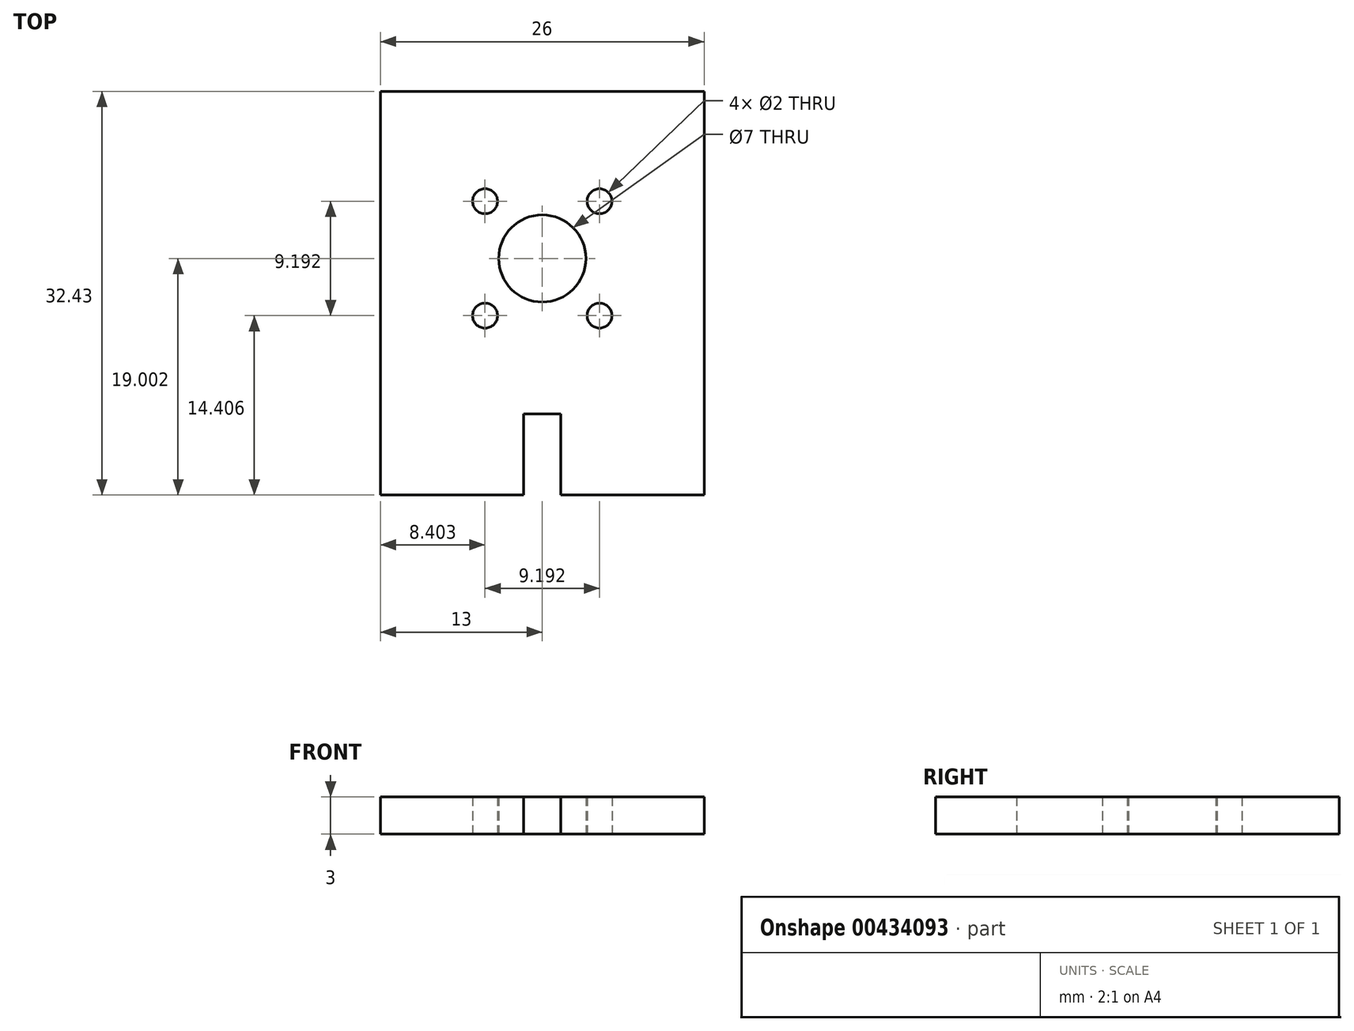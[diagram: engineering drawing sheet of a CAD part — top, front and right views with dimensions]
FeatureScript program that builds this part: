
annotation { "Feature Type Name" : "Feature", "Feature Type Description" : "" }
export const myFeature = defineFeature(function(context is Context, id is Id, definition is map)
    precondition{}
    {
        {
            var Q0;
            Q0=qCreatedBy(makeId("Top.planeOp"),FACE);
            var sketch = newSketch(context, id + "F0", { "sketchPlane" : qUnion([Q0])});
            skLineSegment(sketch, "E0", {"start": v(-216.4, -193.39) * mm, "end": v(-216.4, -327.3) * mm, "construction": true});
            skLineSegment(sketch, "E1", {"start": v(-237.43, -203.28) * mm, "end": v(-216.4, -203.28) * mm, "construction": true});
            skLineSegment(sketch, "E2", {"start": v(-216.4, -203.28) * mm, "end": v(-758.17, -203.28) * mm});
            skLineSegment(sketch, "E3", {"start": v(-768.17, -213.28) * mm, "end": v(-768.17, -312.5) * mm});
            skLineSegment(sketch, "E4", {"start": v(-216.4, -193.39) * mm, "end": v(-216.4, -56.57) * mm, "construction": true});
            skLineSegment(sketch, "E5", {"start": v(-216.4, -323.28) * mm, "end": v(-755.06, -323.28) * mm});
            skPoint(sketch, "E6.start.orphan", {"position": v(-216.4, -323.28) * mm});
            skLineSegment(sketch, "E7.0", {"start": v(-216.4, -213.28) * mm, "end": v(-768.17, -213.28) * mm});
            skLineSegment(sketch, "E8.0", {"start": v(-216.4, -318.28) * mm, "end": v(-765.68, -318.28) * mm});
            skLineSegment(sketch, "E9", {"start": v(-742.85, -318.28) * mm, "end": v(-742.85, -282.51) * mm});
            skLineSegment(sketch, "E10", {"start": v(-742.85, -282.51) * mm, "end": v(-742.85, -281.59) * mm});
            skLineSegment(sketch, "E11", {"start": v(-204.13, -279.09) * mm, "end": v(-768.17, -279.09) * mm, "construction": true});
            skLineSegment(sketch, "E12.0", {"start": v(-216.4, -276.59) * mm, "end": v(-747.57, -276.59) * mm});
            skLineSegment(sketch, "E13.0", {"start": v(-216.4, -281.59) * mm, "end": v(-747.57, -281.59) * mm});
            skLineSegment(sketch, "E14", {"start": v(-747.57, -281.59) * mm, "end": v(-747.57, -276.59) * mm});
            skLineSegment(sketch, "E15.trimOffspring", {"start": v(-742.85, -276.59) * mm, "end": v(-742.85, -213.28) * mm});
            skArc(sketch, "E16", {"start": v(-768.17, -213.28) * mm, "mid": v(-765.3, -206.28) * mm, "end": v(-758.37, -203.28) * mm});
            skFitSpline(sketch, "E17", {"points": [v(-768.17, -312.5) * mm, v(-767.64, -314.89) * mm, v(-766.5, -317.2) * mm, v(-764.5, -319.48) * mm, v(-762.87, -320.69) * mm, v(-761.52, -321.5) * mm, v(-759.85, -322.26) * mm, v(-758.32, -322.76) * mm, v(-758.3, -322.76) * mm, v(-758.3, -322.78) * mm, v(-755.06, -323.28) * mm], "startDerivative": vector(3.3, -19) * mm, "endDerivative": vector(33.17, -1.34) * mm});
            skLineSegment(sketch, "E18", {"start": v(26.78, 14.29) * mm, "end": v(55.78, 14.29) * mm, "construction": true});
            skLineSegment(sketch, "E19", {"start": v(171.63, -38.26) * mm, "end": v(138.63, -38.26) * mm, "construction": true});
            skLineSegment(sketch, "E20", {"start": v(-20.22, 54.29) * mm, "end": v(-20.22, 14.79) * mm, "construction": true});
            skLineSegment(sketch, "E21", {"start": v(59.78, 18.29) * mm, "end": v(59.78, 54.33) * mm, "construction": true});
            skLineSegment(sketch, "E22", {"start": v(-20.22, 54.29) * mm, "end": v(-16.22, 54.29) * mm, "construction": true});
            skLineSegment(sketch, "E23", {"start": v(-0.22, 58.29) * mm, "end": v(-0.22, 4.66) * mm, "construction": true});
            skPoint(sketch, "E23.endSnap0", {"position": v(-0.22, 54.29) * mm});
            skLineSegment(sketch, "E24", {"start": v(-16.22, 10.79) * mm, "end": v(15.78, 10.79) * mm, "construction": true});
            skPoint(sketch, "E25.startSnap0", {"position": v(20.78, 58.29) * mm});
            skLineSegment(sketch, "E26", {"start": v(19.78, 54.29) * mm, "end": v(19.78, 14.79) * mm, "construction": true});
            skPoint(sketch, "E27.0.start.orphan", {"position": v(19.78, 58.29) * mm});
            skLineSegment(sketch, "E28.0", {"start": v(-16.22, 57.79) * mm, "end": v(-16.22, 54.29) * mm});
            skLineSegment(sketch, "E29", {"start": v(-16.22, 57.79) * mm, "end": v(-16.22, 54.29) * mm, "construction": true});
            skPoint(sketch, "E30.orphan", {"position": v(-16.22, -36.82) * mm});
            skLineSegment(sketch, "E31.trimOffspring", {"start": v(-16.22, 10.79) * mm, "end": v(-16.22, 10.48) * mm, "construction": true});
            skLineSegment(sketch, "E32.trimOffspring", {"start": v(-16.22, 10.79) * mm, "end": v(-16.22, 10.48) * mm});
            skLineSegment(sketch, "E33.MirrorCS", {"start": v(15.78, 57.79) * mm, "end": v(15.78, 54.29) * mm, "construction": true});
            skLineSegment(sketch, "E34.0", {"start": v(-20.22, 14.79) * mm, "end": v(-16.22, 14.79) * mm});
            skLineSegment(sketch, "E35", {"start": v(-16.22, 14.79) * mm, "end": v(-16.22, 10.48) * mm, "construction": true});
            skLineSegment(sketch, "E36", {"start": v(15.78, 14.79) * mm, "end": v(15.78, 10.79) * mm, "construction": true});
            skLineSegment(sketch, "E37.trimOffspring", {"start": v(15.78, 14.79) * mm, "end": v(19.78, 14.79) * mm});
            skLineSegment(sketch, "E38.trimOffspring", {"start": v(15.78, 54.29) * mm, "end": v(19.78, 54.29) * mm, "construction": true});
            skLineSegment(sketch, "E39", {"start": v(-0.22, 51.23) * mm, "end": v(-8.97, 51.23) * mm});
            skLineSegment(sketch, "E40", {"start": v(-8.97, 51.23) * mm, "end": v(-12.82, 47.31) * mm});
            skLineSegment(sketch, "E41", {"start": v(-12.82, 47.31) * mm, "end": v(-12.82, 34.54) * mm});
            skLineSegment(sketch, "E42", {"start": v(19.78, 34.54) * mm, "end": v(-20.22, 34.54) * mm, "construction": true});
            skLineSegment(sketch, "E43.MirrorCS", {"start": v(-0.22, 51.23) * mm, "end": v(8.53, 51.23) * mm});
            skLineSegment(sketch, "E44.MirrorCS", {"start": v(8.53, 51.23) * mm, "end": v(12.38, 47.31) * mm});
            skLineSegment(sketch, "E45.MirrorCS", {"start": v(12.38, 47.31) * mm, "end": v(12.38, 34.54) * mm});
            skLineSegment(sketch, "E46.MirrorCS", {"start": v(-0.22, 17.85) * mm, "end": v(8.53, 17.85) * mm});
            skLineSegment(sketch, "E47.MirrorCS", {"start": v(-0.22, 17.85) * mm, "end": v(-8.97, 17.85) * mm});
            skLineSegment(sketch, "E48.MirrorCS", {"start": v(-8.97, 17.85) * mm, "end": v(-12.82, 21.76) * mm});
            skLineSegment(sketch, "E49.MirrorCS", {"start": v(-12.82, 21.76) * mm, "end": v(-12.82, 34.54) * mm});
            skLineSegment(sketch, "E50.MirrorCS", {"start": v(12.38, 21.76) * mm, "end": v(12.38, 34.54) * mm});
            skLineSegment(sketch, "E51.MirrorCS", {"start": v(8.53, 17.85) * mm, "end": v(12.38, 21.76) * mm});
            skLineSegment(sketch, "E52", {"start": v(-16.22, 57.79) * mm, "end": v(15.78, 57.79) * mm});
            skLineSegment(sketch, "E53", {"start": v(15.78, 54.29) * mm, "end": v(19.78, 54.29) * mm});
            skLineSegment(sketch, "E54", {"start": v(19.78, 14.79) * mm, "end": v(15.78, 14.79) * mm});
            skLineSegment(sketch, "E55", {"start": v(15.78, 10.79) * mm, "end": v(-16.22, 10.79) * mm});
            skLineSegment(sketch, "E56", {"start": v(-16.22, 14.79) * mm, "end": v(-20.22, 14.79) * mm});
            skLineSegment(sketch, "E57", {"start": v(-20.22, 54.29) * mm, "end": v(-20.22, 14.79) * mm});
            skLineSegment(sketch, "E58", {"start": v(-20.22, 54.29) * mm, "end": v(-16.22, 54.29) * mm});
            skLineSegment(sketch, "E59", {"start": v(19.78, 54.29) * mm, "end": v(19.78, 14.79) * mm});
            skLineSegment(sketch, "E60", {"start": v(15.78, 54.29) * mm, "end": v(15.78, 57.79) * mm});
            skLineSegment(sketch, "E61", {"start": v(15.78, 14.79) * mm, "end": v(15.78, 10.79) * mm});
            skLineSegment(sketch, "E62", {"start": v(-16.22, 14.79) * mm, "end": v(-16.22, 10.79) * mm});
            skLineSegment(sketch, "E63.0", {"start": v(55.78, 14.29) * mm, "end": v(55.78, 18.29) * mm});
            skLineSegment(sketch, "E64", {"start": v(22.78, 54.3) * mm, "end": v(26.78, 54.3) * mm, "construction": true});
            skLineSegment(sketch, "E65", {"start": v(22.78, 54.3) * mm, "end": v(22.78, 18.29) * mm, "construction": true});
            skLineSegment(sketch, "E66.0", {"start": v(26.78, 58.29) * mm, "end": v(26.78, 54.3) * mm});
            skLineSegment(sketch, "E67.0", {"start": v(22.78, 18.29) * mm, "end": v(26.78, 18.29) * mm});
            skPoint(sketch, "E68.orphan", {"position": v(25.41, 14.29) * mm});
            skLineSegment(sketch, "E69.trimOffspring", {"start": v(26.78, 18.29) * mm, "end": v(26.78, 14.29) * mm});
            skLineSegment(sketch, "E70.trimOffspring", {"start": v(55.78, 54.33) * mm, "end": v(55.78, 58.29) * mm});
            skLineSegment(sketch, "E71.trimOffspring", {"start": v(55.78, 18.29) * mm, "end": v(59.78, 18.29) * mm});
            skLineSegment(sketch, "E72", {"start": v(55.78, 14.29) * mm, "end": v(26.78, 14.29) * mm});
            skLineSegment(sketch, "E73", {"start": v(26.78, 18.29) * mm, "end": v(22.78, 18.29) * mm});
            skLineSegment(sketch, "E74", {"start": v(22.78, 18.29) * mm, "end": v(22.78, 54.3) * mm});
            skLineSegment(sketch, "E75", {"start": v(22.78, 54.3) * mm, "end": v(26.78, 54.3) * mm});
            skLineSegment(sketch, "E76", {"start": v(26.78, 58.29) * mm, "end": v(55.78, 58.29) * mm});
            skLineSegment(sketch, "E77", {"start": v(55.78, 54.33) * mm, "end": v(59.78, 54.33) * mm});
            skLineSegment(sketch, "E78", {"start": v(59.78, 54.33) * mm, "end": v(59.78, 18.75) * mm});
            skLineSegment(sketch, "E79.trimOffspring", {"start": v(55.78, 54.33) * mm, "end": v(59.78, 54.33) * mm, "construction": true});
            skPoint(sketch, "E80.orphan", {"position": v(61.78, 58.29) * mm});
            skLineSegment(sketch, "E81.trimOffspring", {"start": v(26.78, 58.29) * mm, "end": v(55.78, 58.29) * mm, "construction": true});
            skLineSegment(sketch, "E82", {"start": v(41.28, 58.29) * mm, "end": v(41.28, 14.29) * mm, "construction": true});
            skLineSegment(sketch, "E83", {"start": v(41.28, 51.1) * mm, "end": v(34.59, 51.1) * mm});
            skLineSegment(sketch, "E84", {"start": v(34.59, 51.1) * mm, "end": v(30.29, 47.53) * mm});
            skLineSegment(sketch, "E85", {"start": v(30.29, 47.53) * mm, "end": v(30.29, 36.34) * mm});
            skLineSegment(sketch, "E86.MirrorCS", {"start": v(41.28, 51.1) * mm, "end": v(47.97, 51.1) * mm});
            skLineSegment(sketch, "E87.MirrorCS", {"start": v(47.97, 51.1) * mm, "end": v(52.27, 47.53) * mm});
            skPoint(sketch, "E88.start.orphan", {"position": v(59.78, 38.29) * mm});
            skLineSegment(sketch, "E89", {"start": v(22.78, 36.29) * mm, "end": v(59.78, 36.54) * mm, "construction": true});
            skPoint(sketch, "E90.MirrorCS.end.orphan", {"position": v(52.27, 38.29) * mm});
            skPoint(sketch, "E90.MirrorCS.start.orphan", {"position": v(52.27, 47.53) * mm});
            skLineSegment(sketch, "E91", {"start": v(52.27, 47.53) * mm, "end": v(52.35, 36.5) * mm});
            skPoint(sketch, "E92.orphan", {"position": v(30.29, 38.29) * mm});
            skLineSegment(sketch, "E93.MirrorCS", {"start": v(41.48, 21.73) * mm, "end": v(48.18, 21.82) * mm});
            skLineSegment(sketch, "E94.MirrorCS", {"start": v(48.18, 21.82) * mm, "end": v(52.43, 25.45) * mm});
            skLineSegment(sketch, "E95.MirrorCS", {"start": v(52.43, 25.45) * mm, "end": v(52.35, 36.5) * mm});
            skLineSegment(sketch, "E96.MirrorCS", {"start": v(41.48, 21.73) * mm, "end": v(34.8, 21.63) * mm});
            skLineSegment(sketch, "E97.MirrorCS", {"start": v(34.8, 21.63) * mm, "end": v(30.44, 25.15) * mm});
            skLineSegment(sketch, "E98.MirrorCS", {"start": v(30.44, 25.15) * mm, "end": v(30.29, 36.34) * mm});
            skLineSegment(sketch, "E99", {"start": v(62.61, 49.29) * mm, "end": v(62.61, 18.29) * mm, "construction": true});
            skLineSegment(sketch, "E100", {"start": v(95.11, 49.29) * mm, "end": v(95.11, 18.29) * mm, "construction": true});
            skLineSegment(sketch, "E101", {"start": v(66.61, 53.29) * mm, "end": v(90.63, 53.29) * mm, "construction": true});
            skLineSegment(sketch, "E102.trimOffspring", {"start": v(62.61, 18.29) * mm, "end": v(66.61, 18.29) * mm});
            skLineSegment(sketch, "E103.0", {"start": v(91.11, 49.29) * mm, "end": v(95.11, 49.29) * mm});
            skLineSegment(sketch, "E104.0", {"start": v(66.61, 53.29) * mm, "end": v(66.61, 49.29) * mm});
            skLineSegment(sketch, "E105.0", {"start": v(91.11, 53.29) * mm, "end": v(91.11, 49.29) * mm});
            skLineSegment(sketch, "E106.trimOffspring", {"start": v(66.61, 14.29) * mm, "end": v(91.11, 14.29) * mm, "construction": true});
            skLineSegment(sketch, "E107.trimOffspring", {"start": v(91.11, 18.29) * mm, "end": v(95.11, 18.29) * mm});
            skLineSegment(sketch, "E108.trimOffspring", {"start": v(66.61, 18.29) * mm, "end": v(66.61, 14.29) * mm});
            skLineSegment(sketch, "E109.trimOffspring", {"start": v(91.11, 18.29) * mm, "end": v(91.11, 14.29) * mm});
            skLineSegment(sketch, "E110.trimOffspring", {"start": v(62.61, 49.29) * mm, "end": v(66.61, 49.29) * mm});
            skLineSegment(sketch, "E111", {"start": v(66.61, 53.29) * mm, "end": v(90.63, 53.29) * mm});
            skLineSegment(sketch, "E112", {"start": v(95.11, 49.29) * mm, "end": v(95.11, 18.29) * mm});
            skLineSegment(sketch, "E113", {"start": v(62.61, 49.29) * mm, "end": v(62.61, 18.29) * mm});
            skLineSegment(sketch, "E114", {"start": v(66.61, 14.29) * mm, "end": v(91.11, 14.29) * mm});
            skPoint(sketch, "E115.orphan", {"position": v(62.61, 49.98) * mm});
            skPoint(sketch, "E116.endSnap0", {"position": v(97.87, 14.29) * mm});
            skLineSegment(sketch, "E117", {"start": v(99.1, 41.57) * mm, "end": v(99.1, 18.29) * mm, "construction": true});
            skLineSegment(sketch, "E118.0", {"start": v(103.1, 14.29) * mm, "end": v(103.1, 18.29) * mm});
            skLineSegment(sketch, "E119.0", {"start": v(122.6, 14.29) * mm, "end": v(122.6, 18.29) * mm});
            skLineSegment(sketch, "E120.0", {"start": v(99.1, 41.79) * mm, "end": v(103.1, 41.79) * mm});
            skLineSegment(sketch, "E121.0", {"start": v(99.1, 18.29) * mm, "end": v(103.1, 18.29) * mm});
            skPoint(sketch, "E122.orphan", {"position": v(129.13, 14.29) * mm});
            skLineSegment(sketch, "E123.trimOffspring", {"start": v(126.6, 18.29) * mm, "end": v(126.6, 41.79) * mm});
            skLineSegment(sketch, "E124.trimOffspring", {"start": v(103.1, 45.79) * mm, "end": v(122.6, 45.79) * mm});
            skLineSegment(sketch, "E125.trimOffspring", {"start": v(103.1, 41.79) * mm, "end": v(103.1, 45.79) * mm});
            skLineSegment(sketch, "E126.trimOffspring", {"start": v(122.6, 41.79) * mm, "end": v(126.6, 41.79) * mm});
            skLineSegment(sketch, "E127.trimOffspring", {"start": v(122.6, 41.79) * mm, "end": v(122.6, 45.79) * mm});
            skLineSegment(sketch, "E128.trimOffspring", {"start": v(103.1, 14.29) * mm, "end": v(122.6, 14.29) * mm, "construction": true});
            skLineSegment(sketch, "E129.trimOffspring", {"start": v(99.1, 18.29) * mm, "end": v(99.1, 41.79) * mm, "construction": true});
            skLineSegment(sketch, "E130.trimOffspring", {"start": v(122.6, 18.29) * mm, "end": v(126.6, 18.29) * mm});
            skLineSegment(sketch, "E131", {"start": v(103.1, 14.29) * mm, "end": v(122.6, 14.29) * mm});
            skPoint(sketch, "E132.orphan", {"position": v(95.11, 14.29) * mm});
            skPoint(sketch, "E133.orphan", {"position": v(95.11, 49.68) * mm});
            skLineSegment(sketch, "E134", {"start": v(78.62, 53.29) * mm, "end": v(78.62, 14.29) * mm, "construction": true});
            skLineSegment(sketch, "E135", {"start": v(62.61, 33.79) * mm, "end": v(95.11, 33.79) * mm, "construction": true});
            skLineSegment(sketch, "E136", {"start": v(78.62, 47.64) * mm, "end": v(71.14, 47.64) * mm});
            skLineSegment(sketch, "E137", {"start": v(71.14, 47.64) * mm, "end": v(68.95, 45.1) * mm});
            skLineSegment(sketch, "E138", {"start": v(68.95, 45.1) * mm, "end": v(68.95, 33.79) * mm});
            skLineSegment(sketch, "E139.MirrorCS", {"start": v(78.62, 47.64) * mm, "end": v(86.1, 47.64) * mm});
            skLineSegment(sketch, "E140.MirrorCS", {"start": v(86.1, 47.64) * mm, "end": v(88.29, 45.1) * mm});
            skLineSegment(sketch, "E141.MirrorCS", {"start": v(88.29, 45.1) * mm, "end": v(88.29, 33.79) * mm});
            skLineSegment(sketch, "E142.MirrorCS", {"start": v(78.62, 19.94) * mm, "end": v(71.14, 19.94) * mm});
            skLineSegment(sketch, "E143.MirrorCS", {"start": v(71.14, 19.94) * mm, "end": v(68.95, 22.48) * mm});
            skLineSegment(sketch, "E144.MirrorCS", {"start": v(68.95, 22.48) * mm, "end": v(68.95, 33.79) * mm});
            skLineSegment(sketch, "E145.MirrorCS", {"start": v(78.62, 19.94) * mm, "end": v(86.1, 19.94) * mm});
            skLineSegment(sketch, "E146.MirrorCS", {"start": v(86.1, 19.94) * mm, "end": v(88.29, 22.48) * mm});
            skLineSegment(sketch, "E147.MirrorCS", {"start": v(88.29, 22.48) * mm, "end": v(88.29, 33.79) * mm});
            skLineSegment(sketch, "E148", {"start": v(112.85, 45.79) * mm, "end": v(112.85, 14.29) * mm, "construction": true});
            skLineSegment(sketch, "E149", {"start": v(99.1, 30.04) * mm, "end": v(126.6, 30.04) * mm, "construction": true});
            skLineSegment(sketch, "E150", {"start": v(112.85, 39.72) * mm, "end": v(107.14, 39.72) * mm});
            skLineSegment(sketch, "E151", {"start": v(107.14, 39.72) * mm, "end": v(105.12, 37.19) * mm});
            skLineSegment(sketch, "E152", {"start": v(105.12, 37.19) * mm, "end": v(105.12, 30.04) * mm});
            skLineSegment(sketch, "E153.MirrorCS", {"start": v(112.85, 39.72) * mm, "end": v(118.56, 39.72) * mm});
            skLineSegment(sketch, "E154.MirrorCS", {"start": v(118.56, 39.72) * mm, "end": v(120.59, 37.19) * mm});
            skLineSegment(sketch, "E155.MirrorCS", {"start": v(120.59, 37.19) * mm, "end": v(120.59, 30.04) * mm});
            skLineSegment(sketch, "E156.MirrorCS", {"start": v(118.56, 20.35) * mm, "end": v(120.59, 22.89) * mm});
            skLineSegment(sketch, "E157.MirrorCS", {"start": v(112.85, 20.35) * mm, "end": v(118.56, 20.35) * mm});
            skLineSegment(sketch, "E158.MirrorCS", {"start": v(112.85, 20.35) * mm, "end": v(107.14, 20.35) * mm});
            skLineSegment(sketch, "E159.MirrorCS", {"start": v(107.14, 20.35) * mm, "end": v(105.12, 22.89) * mm});
            skLineSegment(sketch, "E160.MirrorCS", {"start": v(105.12, 22.89) * mm, "end": v(105.12, 30.04) * mm});
            skLineSegment(sketch, "E161.MirrorCS", {"start": v(120.59, 22.89) * mm, "end": v(120.59, 30.04) * mm});
            skPoint(sketch, "E162.orphan", {"position": v(22.78, 14.29) * mm});
            skLineSegment(sketch, "E163", {"start": v(-7, 45.54) * mm, "end": v(6.03, 45.54) * mm, "construction": true});
            skLineSegment(sketch, "E164", {"start": v(-10.72, 27.54) * mm, "end": v(-10.72, 41.54) * mm, "construction": true});
            skPoint(sketch, "E164.endSnap0", {"position": v(-12.82, 40.93) * mm});
            skLineSegment(sketch, "E165.MirrorCS", {"start": v(10.28, 27.54) * mm, "end": v(10.28, 41.54) * mm, "construction": true});
            skLineSegment(sketch, "E166.MirrorCS", {"start": v(-7, 23.54) * mm, "end": v(6.03, 23.54) * mm, "construction": true});
            skLineSegment(sketch, "E167.0", {"start": v(-10.72, 41.54) * mm, "end": v(-6.72, 41.54) * mm});
            skLineSegment(sketch, "E168.0", {"start": v(-6.72, 23.54) * mm, "end": v(-6.72, 27.54) * mm});
            skPoint(sketch, "E169.orphan", {"position": v(-10.72, 40.93) * mm});
            skPoint(sketch, "E170.orphan", {"position": v(10.28, 40.93) * mm});
            skLineSegment(sketch, "E171.MirrorCS", {"start": v(-10.72, 27.54) * mm, "end": v(-6.72, 27.54) * mm});
            skLineSegment(sketch, "E172.MirrorCS", {"start": v(6.28, 23.54) * mm, "end": v(6.28, 27.54) * mm});
            skLineSegment(sketch, "E173", {"start": v(-6.72, 45.54) * mm, "end": v(6.03, 45.54) * mm});
            skLineSegment(sketch, "E174", {"start": v(-6.72, 23.54) * mm, "end": v(6.28, 23.54) * mm});
            skLineSegment(sketch, "E175", {"start": v(-10.72, 41.54) * mm, "end": v(-10.72, 27.54) * mm});
            skLineSegment(sketch, "E176.trimOffspring", {"start": v(6.28, 41.54) * mm, "end": v(10.28, 41.54) * mm});
            skLineSegment(sketch, "E177.trimOffspring", {"start": v(-6.72, 41.54) * mm, "end": v(-6.72, 45.54) * mm});
            skLineSegment(sketch, "E178.trimOffspring", {"start": v(6.28, 41.54) * mm, "end": v(6.28, 45.54) * mm});
            skLineSegment(sketch, "E179.trimOffspring", {"start": v(6.28, 27.54) * mm, "end": v(10.28, 27.54) * mm});
            skPoint(sketch, "E180.orphan", {"position": v(-10.72, 26.48) * mm});
            skPoint(sketch, "E181.orphan", {"position": v(10.28, 26.48) * mm});
            skLineSegment(sketch, "E182", {"start": v(10.28, 41.54) * mm, "end": v(10.28, 27.54) * mm});
            skPoint(sketch, "E183.orphan", {"position": v(-20.22, 10.79) * mm});
            skLineSegment(sketch, "E184.trimOffspring", {"start": v(-20.22, -9.83) * mm, "end": v(-20.22, -34.26) * mm, "construction": true});
            skPoint(sketch, "E185.orphan", {"position": v(19.78, 10.79) * mm});
            skLineSegment(sketch, "E186", {"start": v(5.78, -9.83) * mm, "end": v(5.78, -34.26) * mm, "construction": true});
            skLineSegment(sketch, "E187", {"start": v(8.94, -34.33) * mm, "end": v(8.94, 1.17) * mm, "construction": true});
            skLineSegment(sketch, "E188.trimOffspring", {"start": v(1.78, -38.26) * mm, "end": v(-5.72, -38.26) * mm, "construction": true});
            skLineSegment(sketch, "E189", {"start": v(12.94, 5.17) * mm, "end": v(40.94, 5.17) * mm, "construction": true});
            skLineSegment(sketch, "E190", {"start": v(44.94, 1.17) * mm, "end": v(44.94, -34.33) * mm, "construction": true});
            skLineSegment(sketch, "E191", {"start": v(87.34, -34.33) * mm, "end": v(87.34, 6.67) * mm, "construction": true});
            skPoint(sketch, "E192.orphan", {"position": v(88.24, 10.67) * mm});
            skLineSegment(sketch, "E193", {"start": v(94.23, 11.74) * mm, "end": v(127.23, 11.74) * mm, "construction": true});
            skLineSegment(sketch, "E194", {"start": v(131.23, 7.74) * mm, "end": v(131.23, -34.26) * mm, "construction": true});
            skLineSegment(sketch, "E195", {"start": v(90.23, 7.74) * mm, "end": v(90.23, -34.26) * mm, "construction": true});
            skLineSegment(sketch, "E196", {"start": v(134.63, 7.74) * mm, "end": v(134.63, 5.1) * mm, "construction": true});
            skPoint(sketch, "E196.startSnap0", {"position": v(134.63, 11.74) * mm});
            skLineSegment(sketch, "E197", {"start": v(175.63, 7.74) * mm, "end": v(175.63, -34.26) * mm, "construction": true});
            skPoint(sketch, "E198.orphan", {"position": v(93.98, 11.74) * mm});
            skLineSegment(sketch, "E199", {"start": v(134.63, 7.74) * mm, "end": v(134.63, -34.26) * mm, "construction": true});
            skLineSegment(sketch, "E200.trimOffspring", {"start": v(138.63, 11.74) * mm, "end": v(171.63, 11.74) * mm, "construction": true});
            skLineSegment(sketch, "E201.trimOffspring", {"start": v(127.23, -38.26) * mm, "end": v(112.23, -38.26) * mm, "construction": true});
            skLineSegment(sketch, "E202", {"start": v(-7.22, -5.83) * mm, "end": v(-7.22, -38.26) * mm, "construction": true});
            skLineSegment(sketch, "E203", {"start": v(26.94, 5.17) * mm, "end": v(26.94, -38.33) * mm, "construction": true});
            skLineSegment(sketch, "E204", {"start": v(67.17, 10.67) * mm, "end": v(67.34, -38.33) * mm, "construction": true});
            skLineSegment(sketch, "E205", {"start": v(110.73, 11.74) * mm, "end": v(110.73, -38.26) * mm, "construction": true});
            skLineSegment(sketch, "E206", {"start": v(154.96, 11.74) * mm, "end": v(155.13, -38.26) * mm, "construction": true});
            skLineSegment(sketch, "E207.0", {"start": v(109.23, -25.26) * mm, "end": v(109.23, -38.26) * mm, "construction": true});
            skLineSegment(sketch, "E208.0", {"start": v(112.23, -25.26) * mm, "end": v(112.23, -38.26) * mm});
            skLineSegment(sketch, "E209.0", {"start": v(112.23, -25.26) * mm, "end": v(109.23, -25.26) * mm, "construction": true});
            skLineSegment(sketch, "E210", {"start": v(109.23, -38.26) * mm, "end": v(109.23, -25.26) * mm});
            skLineSegment(sketch, "E211", {"start": v(112.23, -25.26) * mm, "end": v(109.23, -25.26) * mm});
            skLineSegment(sketch, "E212.trimOffspring", {"start": v(109.23, -38.26) * mm, "end": v(94.23, -38.26) * mm, "construction": true});
            skLineSegment(sketch, "E213.0", {"start": v(175.63, -34.26) * mm, "end": v(171.63, -34.26) * mm});
            skLineSegment(sketch, "E214.0", {"start": v(171.63, 11.74) * mm, "end": v(171.63, 7.74) * mm, "construction": true});
            skLineSegment(sketch, "E215.0", {"start": v(134.63, 7.74) * mm, "end": v(138.63, 7.74) * mm, "construction": true});
            skLineSegment(sketch, "E216.0", {"start": v(138.63, 11.74) * mm, "end": v(138.63, 7.74) * mm, "construction": true});
            skLineSegment(sketch, "E217.trimOffspring", {"start": v(171.63, 7.74) * mm, "end": v(175.63, 7.74) * mm, "construction": true});
            skLineSegment(sketch, "E218.trimOffspring", {"start": v(138.63, -34.26) * mm, "end": v(134.63, -34.26) * mm});
            skLineSegment(sketch, "E219.trimOffspring", {"start": v(138.63, -34.26) * mm, "end": v(138.63, -38.26) * mm, "construction": true});
            skLineSegment(sketch, "E220.trimOffspring", {"start": v(171.63, -34.26) * mm, "end": v(171.63, -38.26) * mm, "construction": true});
            skPoint(sketch, "E221.orphan", {"position": v(175.28, 11.74) * mm});
            skPoint(sketch, "E222.orphan", {"position": v(175.63, 11.74) * mm});
            skPoint(sketch, "E223.orphan", {"position": v(134.63, -38.26) * mm});
            skPoint(sketch, "E224.orphan", {"position": v(175.63, -38.26) * mm});
            skLineSegment(sketch, "E225.0", {"start": v(127.23, 11.74) * mm, "end": v(127.23, 7.74) * mm});
            skLineSegment(sketch, "E226.0", {"start": v(94.23, 11.74) * mm, "end": v(94.23, 7.74) * mm});
            skLineSegment(sketch, "E227.0", {"start": v(90.23, 7.74) * mm, "end": v(94.23, 7.74) * mm, "construction": true});
            skLineSegment(sketch, "E228.0", {"start": v(94.23, -34.26) * mm, "end": v(90.23, -34.26) * mm, "construction": true});
            skLineSegment(sketch, "E229.0", {"start": v(131.23, -34.26) * mm, "end": v(127.23, -34.26) * mm, "construction": true});
            skLineSegment(sketch, "E230.trimOffspring", {"start": v(127.23, 7.74) * mm, "end": v(131.23, 7.74) * mm, "construction": true});
            skLineSegment(sketch, "E231.trimOffspring", {"start": v(94.23, -34.26) * mm, "end": v(94.23, -38.26) * mm});
            skPoint(sketch, "E232.orphan", {"position": v(90.23, -38.26) * mm});
            skPoint(sketch, "E233.orphan", {"position": v(90.23, 11.74) * mm});
            skPoint(sketch, "E234.orphan", {"position": v(131.23, 11.74) * mm});
            skLineSegment(sketch, "E235", {"start": v(94.23, -38.26) * mm, "end": v(109.23, -38.26) * mm});
            skLineSegment(sketch, "E236", {"start": v(90.23, 7.74) * mm, "end": v(90.23, -34.26) * mm});
            skLineSegment(sketch, "E237", {"start": v(90.23, -34.26) * mm, "end": v(94.23, -34.26) * mm});
            skLineSegment(sketch, "E238", {"start": v(127.23, -34.26) * mm, "end": v(131.23, -34.26) * mm});
            skLineSegment(sketch, "E239", {"start": v(131.23, -34.26) * mm, "end": v(131.23, 7.74) * mm});
            skLineSegment(sketch, "E240", {"start": v(131.23, 7.74) * mm, "end": v(127.23, 7.74) * mm});
            skLineSegment(sketch, "E241", {"start": v(94.23, 11.74) * mm, "end": v(127.23, 11.74) * mm});
            skPoint(sketch, "E242.orphan", {"position": v(131.23, -38.26) * mm});
            skLineSegment(sketch, "E243.trimOffspring", {"start": v(127.23, -34.26) * mm, "end": v(127.23, -38.26) * mm});
            skLineSegment(sketch, "E244.trimOffspring", {"start": v(112.23, -38.26) * mm, "end": v(127.23, -38.26) * mm});
            skLineSegment(sketch, "E245", {"start": v(138.63, 11.74) * mm, "end": v(171.63, 11.74) * mm});
            skLineSegment(sketch, "E246", {"start": v(171.63, 7.74) * mm, "end": v(175.63, 7.74) * mm});
            skLineSegment(sketch, "E247", {"start": v(175.63, 7.74) * mm, "end": v(175.63, -34.26) * mm});
            skLineSegment(sketch, "E248", {"start": v(138.63, -38.26) * mm, "end": v(171.63, -38.26) * mm});
            skLineSegment(sketch, "E249", {"start": v(171.63, -38.26) * mm, "end": v(171.63, -34.26) * mm});
            skLineSegment(sketch, "E250", {"start": v(138.63, -38.26) * mm, "end": v(138.63, -34.26) * mm});
            skLineSegment(sketch, "E251", {"start": v(134.63, -34.26) * mm, "end": v(134.63, 7.74) * mm});
            skLineSegment(sketch, "E252", {"start": v(138.63, 7.74) * mm, "end": v(138.63, 11.74) * mm});
            skLineSegment(sketch, "E253", {"start": v(94.23, 7.74) * mm, "end": v(90.23, 7.74) * mm});
            skLineSegment(sketch, "E254", {"start": v(138.63, 7.74) * mm, "end": v(134.63, 7.74) * mm});
            skLineSegment(sketch, "E255", {"start": v(171.63, 7.74) * mm, "end": v(171.63, 11.74) * mm});
            skLineSegment(sketch, "E256", {"start": v(54.82, -17.76) * mm, "end": v(79.71, -17.68) * mm, "construction": true});
            skLineSegment(sketch, "E257", {"start": v(141.1, -17.47) * mm, "end": v(141.04, 1.05) * mm});
            skLineSegment(sketch, "E258", {"start": v(141.04, 1.05) * mm, "end": v(144.02, 4.5) * mm});
            skLineSegment(sketch, "E259", {"start": v(144.02, 4.5) * mm, "end": v(154.98, 4.5) * mm});
            skLineSegment(sketch, "E260", {"start": v(141.1, -17.47) * mm, "end": v(155.06, -17.47) * mm});
            skLineSegment(sketch, "E261.trimOffspring", {"start": v(141.1, -17.47) * mm, "end": v(167.9, -17.38) * mm, "construction": true});
            skLineSegment(sketch, "E262.trimOffspring", {"start": v(97.04, -17.62) * mm, "end": v(110.73, -17.57) * mm, "construction": true});
            skLineSegment(sketch, "E263.MirrorCS", {"start": v(169, -17.37) * mm, "end": v(155.06, -17.47) * mm});
            skLineSegment(sketch, "E264.MirrorCS", {"start": v(169, -17.37) * mm, "end": v(168.94, 1.14) * mm});
            skLineSegment(sketch, "E265.MirrorCS", {"start": v(168.94, 1.14) * mm, "end": v(165.94, 4.57) * mm});
            skLineSegment(sketch, "E266", {"start": v(110.73, -17.57) * mm, "end": v(97.04, -17.62) * mm});
            skLineSegment(sketch, "E267", {"start": v(97.04, 1.2) * mm, "end": v(99.73, 4.04) * mm});
            skLineSegment(sketch, "E268", {"start": v(99.73, 4.04) * mm, "end": v(110.73, 4.04) * mm});
            skPoint(sketch, "E269.orphan", {"position": v(90.23, -17.64) * mm});
            skPoint(sketch, "E270.orphan", {"position": v(131.23, -17.5) * mm});
            skLineSegment(sketch, "E271.MirrorCS", {"start": v(124.42, -17.62) * mm, "end": v(110.73, -17.57) * mm, "construction": true});
            skLineSegment(sketch, "E272.MirrorCS", {"start": v(124.42, 1.2) * mm, "end": v(121.73, 4.04) * mm});
            skLineSegment(sketch, "E273.MirrorCS", {"start": v(121.73, 4.04) * mm, "end": v(110.73, 4.04) * mm});
            skLineSegment(sketch, "E274", {"start": v(110.73, -17.57) * mm, "end": v(124.42, -17.62) * mm});
            skLineSegment(sketch, "E275", {"start": v(26.94, -17.83) * mm, "end": v(39.1, -17.83) * mm});
            skLineSegment(sketch, "E276", {"start": v(39.1, -17.83) * mm, "end": v(38.91, -3.53) * mm});
            skLineSegment(sketch, "E277", {"start": v(38.91, -3.53) * mm, "end": v(36.54, -1) * mm});
            skLineSegment(sketch, "E278", {"start": v(36.54, -1) * mm, "end": v(26.94, -1) * mm});
            skLineSegment(sketch, "E279.MirrorCS", {"start": v(17.33, -1) * mm, "end": v(26.94, -1) * mm});
            skLineSegment(sketch, "E280", {"start": v(14.77, -17.83) * mm, "end": v(26.94, -17.83) * mm});
            skLineSegment(sketch, "E281.trimOffspring", {"start": v(39.1, -17.83) * mm, "end": v(14.77, -17.83) * mm, "construction": true});
            skLineSegment(sketch, "E282", {"start": v(54.76, 1.56) * mm, "end": v(57.89, 4.85) * mm});
            skLineSegment(sketch, "E283", {"start": v(57.89, 4.85) * mm, "end": v(67.2, 4.85) * mm});
            skLineSegment(sketch, "E284.MirrorCS", {"start": v(76.5, 4.91) * mm, "end": v(67.2, 4.85) * mm});
            skLineSegment(sketch, "E285.MirrorCS", {"start": v(79.65, 1.65) * mm, "end": v(76.5, 4.91) * mm});
            skLineSegment(sketch, "E286.MirrorCS", {"start": v(79.71, -17.68) * mm, "end": v(54.82, -17.76) * mm, "construction": true});
            skLineSegment(sketch, "E287", {"start": v(54.82, -17.76) * mm, "end": v(79.71, -17.68) * mm});
            skPoint(sketch, "E288.orphan", {"position": v(47.2, -17.79) * mm});
            skPoint(sketch, "E289.orphan", {"position": v(87.34, -17.65) * mm});
            skLineSegment(sketch, "E290.0", {"start": v(87.34, -34.33) * mm, "end": v(83.34, -34.33) * mm});
            skLineSegment(sketch, "E291.0", {"start": v(51.34, -38.3) * mm, "end": v(51.31, -34.33) * mm});
            skLineSegment(sketch, "E292.0", {"start": v(83.34, -38.33) * mm, "end": v(83.34, -34.33) * mm});
            skLineSegment(sketch, "E293.0", {"start": v(47, 6.67) * mm, "end": v(51.03, 6.67) * mm});
            skLineSegment(sketch, "E294", {"start": v(87.34, 6.67) * mm, "end": v(87.34, -34.33) * mm});
            skPoint(sketch, "E295.orphan", {"position": v(47, 10.67) * mm});
            skPoint(sketch, "E296.orphan", {"position": v(87.34, 10.67) * mm});
            skLineSegment(sketch, "E297.trimOffspring", {"start": v(83.34, 6.67) * mm, "end": v(87.34, 6.67) * mm});
            skLineSegment(sketch, "E298.trimOffspring", {"start": v(83.34, 6.67) * mm, "end": v(83.34, 10.67) * mm});
            skLineSegment(sketch, "E299.trimOffspring", {"start": v(51.03, 6.67) * mm, "end": v(51, 10.7) * mm});
            skLineSegment(sketch, "E300.trimOffspring", {"start": v(51.31, -34.33) * mm, "end": v(47.34, -34.33) * mm});
            skLineSegment(sketch, "E301.0", {"start": v(68.67, 10.68) * mm, "end": v(68.67, 10.67) * mm});
            skLineSegment(sketch, "E302.0", {"start": v(8.94, 1.17) * mm, "end": v(12.94, 1.17) * mm});
            skLineSegment(sketch, "E303.0", {"start": v(44.94, -34.33) * mm, "end": v(40.94, -34.33) * mm});
            skLineSegment(sketch, "E304.0", {"start": v(40.94, 5.17) * mm, "end": v(40.94, 1.17) * mm});
            skLineSegment(sketch, "E305.0", {"start": v(12.94, -38.33) * mm, "end": v(12.94, -34.33) * mm, "construction": true});
            skLineSegment(sketch, "E306", {"start": v(12.94, 5.17) * mm, "end": v(40.94, 5.17) * mm});
            skLineSegment(sketch, "E307", {"start": v(44.94, 1.17) * mm, "end": v(44.94, -34.33) * mm});
            skLineSegment(sketch, "E308", {"start": v(8.94, 1.17) * mm, "end": v(8.94, -34.33) * mm});
            skLineSegment(sketch, "E309.trimOffspring", {"start": v(40.94, 1.17) * mm, "end": v(44.94, 1.17) * mm});
            skLineSegment(sketch, "E310.trimOffspring", {"start": v(40.94, -34.33) * mm, "end": v(40.94, -38.33) * mm});
            skLineSegment(sketch, "E311.trimOffspring", {"start": v(12.94, 1.17) * mm, "end": v(12.94, 5.17) * mm, "construction": true});
            skLineSegment(sketch, "E312.trimOffspring", {"start": v(65.84, -38.33) * mm, "end": v(63.55, -38.33) * mm, "construction": true});
            skPoint(sketch, "E313.orphan", {"position": v(87.34, -38.33) * mm});
            skLineSegment(sketch, "E314", {"start": v(68.84, -38.32) * mm, "end": v(83.34, -38.33) * mm});
            skLineSegment(sketch, "E315", {"start": v(51.34, -38.3) * mm, "end": v(65.84, -38.33) * mm});
            skLineSegment(sketch, "E316", {"start": v(5.78, -5.83) * mm, "end": v(5.78, -38.26) * mm});
            skLineSegment(sketch, "E317", {"start": v(-20.22, -5.83) * mm, "end": v(-20.22, -38.26) * mm});
            skLineSegment(sketch, "E318", {"start": v(-20.22, -38.26) * mm, "end": v(-8.72, -38.26) * mm});
            skPoint(sketch, "E319.orphan", {"position": v(-20.22, -5.83) * mm});
            skPoint(sketch, "E320.orphan", {"position": v(5.78, -5.83) * mm});
            skPoint(sketch, "E321.orphan", {"position": v(-20.22, -38.26) * mm});
            skPoint(sketch, "E322.orphan", {"position": v(5.78, -38.26) * mm});
            skLineSegment(sketch, "E323.0", {"start": v(-8.72, -31.76) * mm, "end": v(-8.72, -38.26) * mm});
            skLineSegment(sketch, "E324.0", {"start": v(-5.72, -31.76) * mm, "end": v(-5.72, -38.26) * mm});
            skLineSegment(sketch, "E325", {"start": v(65.8, -25.33) * mm, "end": v(68.8, -25.33) * mm, "construction": true});
            skLineSegment(sketch, "E326", {"start": v(25.44, -27.33) * mm, "end": v(28.44, -27.33) * mm, "construction": true});
            skLineSegment(sketch, "E327", {"start": v(-8.72, -31.76) * mm, "end": v(-5.72, -31.76) * mm, "construction": true});
            skLineSegment(sketch, "E328.trimOffspring", {"start": v(28.44, -27.33) * mm, "end": v(28.44, -38.33) * mm});
            skLineSegment(sketch, "E329.trimOffspring", {"start": v(25.44, -27.33) * mm, "end": v(25.44, -38.33) * mm});
            skPoint(sketch, "E330.orphan", {"position": v(21.9, -27.33) * mm});
            skPoint(sketch, "E331.orphan", {"position": v(59.95, -25.33) * mm});
            skLineSegment(sketch, "E332.trimOffspring", {"start": v(65.8, -25.33) * mm, "end": v(65.84, -38.33) * mm});
            skLineSegment(sketch, "E333.trimOffspring", {"start": v(68.8, -25.33) * mm, "end": v(68.84, -38.32) * mm});
            skPoint(sketch, "E334.orphan", {"position": v(-12.31, -31.76) * mm});
            skLineSegment(sketch, "E335.trimOffspring", {"start": v(-8.72, -38.26) * mm, "end": v(-16.22, -38.26) * mm, "construction": true});
            skLineSegment(sketch, "E336.trimOffspring", {"start": v(-5.72, -38.26) * mm, "end": v(5.78, -38.26) * mm});
            skPoint(sketch, "E337.orphan", {"position": v(44.94, -38.33) * mm});
            skPoint(sketch, "E338.orphan", {"position": v(8.94, -38.33) * mm});
            skLineSegment(sketch, "E339", {"start": v(12.94, -38.33) * mm, "end": v(25.44, -38.33) * mm});
            skLineSegment(sketch, "E340.trimOffspring", {"start": v(12.94, -34.33) * mm, "end": v(8.94, -34.33) * mm});
            skLineSegment(sketch, "E341", {"start": v(28.44, -38.33) * mm, "end": v(40.94, -38.33) * mm});
            skLineSegment(sketch, "E342", {"start": v(25.44, -27.33) * mm, "end": v(28.44, -27.33) * mm});
            skLineSegment(sketch, "E343", {"start": v(-5.72, -31.76) * mm, "end": v(-8.72, -31.76) * mm});
            skPoint(sketch, "E344.MirrorCS.end.orphan", {"position": v(79.65, 1.65) * mm});
            skPoint(sketch, "E345.MirrorCS.end.orphan", {"position": v(124.42, 1.2) * mm});
            skPoint(sketch, "E345.MirrorCS.start.orphan", {"position": v(124.42, -17.62) * mm});
            skPoint(sketch, "E346.orphan", {"position": v(44.94, 5.17) * mm});
            skPoint(sketch, "E347.orphan", {"position": v(8.94, 5.17) * mm});
            skLineSegment(sketch, "E348", {"start": v(51, 10.7) * mm, "end": v(83.34, 10.67) * mm});
            skPoint(sketch, "E349.MirrorCS.end.orphan", {"position": v(14.96, -3.53) * mm});
            skPoint(sketch, "E350.MirrorCS.end.orphan", {"position": v(17.33, -1) * mm});
            skLineSegment(sketch, "E351.MirrorCS", {"start": v(14.96, -3.53) * mm, "end": v(17.33, -1) * mm});
            skLineSegment(sketch, "E352.MirrorCS", {"start": v(14.77, -17.83) * mm, "end": v(14.96, -3.53) * mm});
            skLineSegment(sketch, "E353", {"start": v(54.76, 1.56) * mm, "end": v(54.82, -17.76) * mm});
            skLineSegment(sketch, "E354.MirrorCS", {"start": v(79.65, 1.65) * mm, "end": v(79.71, -17.68) * mm});
            skPoint(sketch, "E355.orphan", {"position": v(22.78, 58.29) * mm});
            skPoint(sketch, "E356.orphan", {"position": v(59.78, 58.29) * mm});
            skPoint(sketch, "E357.start.orphan", {"position": v(-20.22, 58.29) * mm});
            skLineSegment(sketch, "E358", {"start": v(97.04, -17.62) * mm, "end": v(97.04, 1.2) * mm});
            skLineSegment(sketch, "E359.MirrorCS", {"start": v(124.42, -17.62) * mm, "end": v(124.42, 1.2) * mm});
            skPoint(sketch, "E360.start.orphan", {"position": v(47.34, -38.33) * mm});
            skLineSegment(sketch, "E361", {"start": v(47, 6.67) * mm, "end": v(47.34, -34.33) * mm});
            skLineSegment(sketch, "E362", {"start": v(-330.23, 39.4) * mm, "end": v(-330.23, 36.02) * mm});
            skLineSegment(sketch, "E363", {"start": v(-330.23, 36.02) * mm, "end": v(-320.69, 24.87) * mm});
            skLineSegment(sketch, "E364", {"start": v(-320.69, 24.87) * mm, "end": v(-258.68, 20.34) * mm});
            skFitSpline(sketch, "E365", {"points": [v(-35.67, 50.42) * mm, v(-37.63, 47.25) * mm, v(-41.34, 43.16) * mm, v(-49.6, 37.95) * mm, v(-65.12, 31.76) * mm, v(-84.88, 26.46) * mm, v(-110.2, 22.46) * mm, v(-134.87, 20.11) * mm, v(-163.68, 18.43) * mm, v(-188.05, 17.72) * mm, v(-212.41, 18.01) * mm, v(-232.41, 19.01) * mm], "startDerivative": vector(-42.45, -73.75) * mm, "endDerivative": vector(-183.1, 14.08) * mm});
            skLineSegment(sketch, "E366", {"start": v(-80.23, 38.7) * mm, "end": v(-126.43, 38.7) * mm});
            skLineSegment(sketch, "E367", {"start": v(-126.43, 38.7) * mm, "end": v(-272.1, 44.42) * mm});
            skLineSegment(sketch, "E368", {"start": v(-272.1, 44.42) * mm, "end": v(-330.23, 39.4) * mm});
            skPoint(sketch, "E369.18.internal.orphan", {"position": v(-249.5, 20.34) * mm});
            skLineSegment(sketch, "E370", {"start": v(-232.41, 19.01) * mm, "end": v(-235.3, 19.01) * mm});
            skLineSegment(sketch, "E371", {"start": v(-235.3, 19.01) * mm, "end": v(-243.06, 19.31) * mm});
            skLineSegment(sketch, "E372", {"start": v(-243.06, 19.31) * mm, "end": v(-248.02, 19.57) * mm});
            skLineSegment(sketch, "E373", {"start": v(-248.02, 19.57) * mm, "end": v(-250.7, 19.57) * mm});
            skLineSegment(sketch, "E374", {"start": v(-250.7, 19.57) * mm, "end": v(-249.5, 20.34) * mm});
            skLineSegment(sketch, "E375", {"start": v(-247.85, 20.81) * mm, "end": v(-249.5, 20.34) * mm});
            skPoint(sketch, "E376.4.internal.snap0", {"position": v(-239.18, 19.16) * mm});
            skFitSpline(sketch, "E376", {"points": [v(-247.85, 20.81) * mm, v(-240.36, 22.51) * mm, v(-239.04, 23.25) * mm, v(-238.83, 24) * mm, v(-239.18, 24.62) * mm, v(-241.06, 25.26) * mm, v(-244.33, 25.22) * mm, v(-246.32, 24.97) * mm, v(-251.11, 23.65) * mm, v(-254.24, 22.28) * mm, v(-257.2, 20.81) * mm, v(-258.68, 20.34) * mm], "startDerivative": vector(56.29, 11.43) * mm, "endDerivative": vector(-19, -4.82) * mm});
            skLineSegment(sketch, "E377", {"start": v(154.98, 4.5) * mm, "end": v(165.94, 4.57) * mm});
            skPoint(sketch, "E378.MirrorCS.end.orphan", {"position": v(59.78, 65.67) * mm});
            skPoint(sketch, "E378.MirrorCS.start.orphan", {"position": v(22.78, 65.92) * mm});
            skLineSegment(sketch, "E379", {"start": v(-20.22, -19.26) * mm, "end": v(2.24, -19.26) * mm, "construction": true});
            skCircle(sketch, "E380", {"center": v(-7.22, -19.26) * mm, "radius": 6.5 * mm});
            skCircle(sketch, "E381", {"center": v(-7.22, -19.26) * mm, "radius": 3.5 * mm});
            skLineSegment(sketch, "E382.0", {"start": v(-731.67, 84.36) * mm, "end": v(-698.05, 84.36) * mm, "construction": true});
            skLineSegment(sketch, "E383", {"start": v(-722.98, 93.36) * mm, "end": v(-704.98, 93.36) * mm});
            skLineSegment(sketch, "E384.MirrorCS", {"start": v(-722.98, 75.36) * mm, "end": v(-704.98, 75.36) * mm});
            skLineSegment(sketch, "E385", {"start": v(-7.22, -19.26) * mm, "end": v(-1.53, -13.56) * mm, "construction": true});
            skLineSegment(sketch, "E386", {"start": v(-7.22, -19.26) * mm, "end": v(-15.5, -27.53) * mm, "construction": true});
            skLineSegment(sketch, "E387", {"start": v(-7.22, -19.26) * mm, "end": v(-11.23, -15.25) * mm, "construction": true});
            skLineSegment(sketch, "E388", {"start": v(-7.22, -19.26) * mm, "end": v(0.88, -27.35) * mm, "construction": true});
            skCircle(sketch, "E389", {"center": v(-11.82, -14.66) * mm, "radius": 1 * mm});
            skCircle(sketch, "E390", {"center": v(-11.82, -23.85) * mm, "radius": 1 * mm});
            skCircle(sketch, "E391", {"center": v(-2.62, -23.85) * mm, "radius": 1 * mm});
            skCircle(sketch, "E392", {"center": v(-2.62, -14.66) * mm, "radius": 1 * mm});
            skLineSegment(sketch, "E393", {"start": v(-726.88, 66.69) * mm, "end": v(-715.4, 66.69) * mm, "construction": true});
            skPoint(sketch, "E394.0.start.orphan", {"position": v(-16.22, -5.83) * mm});
            skPoint(sketch, "E395.orphan", {"position": v(-25.3, -19.26) * mm});
            skLineSegment(sketch, "E396", {"start": v(-20.22, -5.83) * mm, "end": v(5.78, -5.83) * mm});
            skPoint(sketch, "E397.end.orphan", {"position": v(-698.05, 98.7) * mm});
            skLineSegment(sketch, "E398", {"start": v(-722.98, 93.36) * mm, "end": v(-722.98, 75.36) * mm});
            skPoint(sketch, "E399.orphan", {"position": v(-728.93, 93.36) * mm});
            skPoint(sketch, "E400.orphan", {"position": v(-728.93, 75.36) * mm});
            skLineSegment(sketch, "E401.0", {"start": v(-704.98, 93.36) * mm, "end": v(-704.98, 75.36) * mm});
            skPoint(sketch, "E402.orphan", {"position": v(-698.05, 93.36) * mm});
            skPoint(sketch, "E403.orphan", {"position": v(-698.05, 75.36) * mm});
            skLineSegment(sketch, "E404", {"start": v(-770.15, 100.7) * mm, "end": v(-770.15, 59.46) * mm});
            skPoint(sketch, "E405.orphan", {"position": v(-75.13, 21.08) * mm});
            skLineSegment(sketch, "E406", {"start": v(-724.49, 106.87) * mm, "end": v(-724.49, 58.9) * mm});
            skLineSegment(sketch, "E407", {"start": v(-476.34, 104.5) * mm, "end": v(-476.34, 41.32) * mm});
            skLineSegment(sketch, "E408.0", {"start": v(-80.23, 39.4) * mm, "end": v(-80.23, 36.02) * mm});
            skLineSegment(sketch, "E409", {"start": v(-80.23, 36.02) * mm, "end": v(-80.23, 27.49) * mm});
            skPoint(sketch, "E410.orphan", {"position": v(55.78, 60.82) * mm});
            skLineSegment(sketch, "E411", {"start": v(26.78, 54.3) * mm, "end": v(26.78, 58.29) * mm});
            skLineSegment(sketch, "E412", {"start": v(55.78, 58.29) * mm, "end": v(55.78, 54.33) * mm});
            skLineSegment(sketch, "E413", {"start": v(59.78, 54.33) * mm, "end": v(59.78, 18.29) * mm});
            skLineSegment(sketch, "E414", {"start": v(91.11, 53.29) * mm, "end": v(90.63, 53.29) * mm});
            skLineSegment(sketch, "E415", {"start": v(99.1, 41.79) * mm, "end": v(99.1, 41.57) * mm});
            skLineSegment(sketch, "E416", {"start": v(99.1, 18.29) * mm, "end": v(99.1, 41.79) * mm});
            skLineSegment(sketch, "E417", {"start": v(65.8, -25.33) * mm, "end": v(68.8, -25.33) * mm});
            skLineSegment(sketch, "E418", {"start": v(12.94, 1.17) * mm, "end": v(12.94, 5.17) * mm});
            skLineSegment(sketch, "E419", {"start": v(12.94, -34.33) * mm, "end": v(12.94, -38.33) * mm});
            skLineSegment(sketch, "E420", {"start": v(14.96, -3.53) * mm, "end": v(14.77, -17.83) * mm});
            skLineSegment(sketch, "E421", {"start": v(17.33, -1) * mm, "end": v(14.96, -3.53) * mm});
            skLineSegment(sketch, "E422", {"start": v(17.33, -1) * mm, "end": v(36.54, -1) * mm});
            skLineSegment(sketch, "E423", {"start": v(12.94, 5.17) * mm, "end": v(12.94, 1.17) * mm});
            skLineSegment(sketch, "E424", {"start": v(12.94, 1.17) * mm, "end": v(8.94, 1.17) * mm});
            skLineSegment(sketch, "E425", {"start": v(8.94, -34.33) * mm, "end": v(12.94, -34.33) * mm});
            skLineSegment(sketch, "E426", {"start": v(25.44, -38.33) * mm, "end": v(25.44, -27.33) * mm});
            skLineSegment(sketch, "E427", {"start": v(40.94, -38.33) * mm, "end": v(40.94, -34.33) * mm});
            skLineSegment(sketch, "E428", {"start": v(40.94, -34.33) * mm, "end": v(44.94, -34.33) * mm});
            skLineSegment(sketch, "E429", {"start": v(39.1, -17.83) * mm, "end": v(14.77, -17.83) * mm});
            skLineSegment(sketch, "E430", {"start": v(-6.72, 45.54) * mm, "end": v(-6.72, 41.54) * mm});
            skLineSegment(sketch, "E431", {"start": v(6.28, 23.54) * mm, "end": v(-6.72, 23.54) * mm});
            skLineSegment(sketch, "E432", {"start": v(-6.72, 27.54) * mm, "end": v(-6.72, 23.54) * mm});
            skLineSegment(sketch, "E433", {"start": v(-6.72, 27.54) * mm, "end": v(-10.72, 27.54) * mm});
            skLineSegment(sketch, "E434", {"start": v(6.28, 45.54) * mm, "end": v(6.03, 45.54) * mm});
            skPoint(sketch, "E435.end.orphan", {"position": v(1.78, -9.83) * mm});
            skPoint(sketch, "E436.orphan", {"position": v(1.78, -5.83) * mm});
            skSolve(sketch);
        }
        {
            var Q0;
            Q0=makeQuery(id+"F0.imprint","IMPRINT",FACE,{"disambiguationData":[TD([[makeQuery(id+"F0.imprint","IMPRINT",EDGE,{"derivedFrom":sQuery(id+"F0.wireOp",EDGE,"E316")}),-1.0]])]});
            var Q1;
            Q1=makeQuery(id+"F0.imprint","IMPRINT",FACE,{"disambiguationData":[TD([[makeQuery(id+"F0.imprint","IMPRINT",EDGE,{"derivedFrom":sQuery(id+"F0.wireOp",EDGE,"E381")}),-1.0]])]});
            extrude(context, id + "F1", {"entities" : qUnion([Q0, Q1]), "depth" : 3 * mm, "offsetDistance" : 25 * mm});
        }
    });
